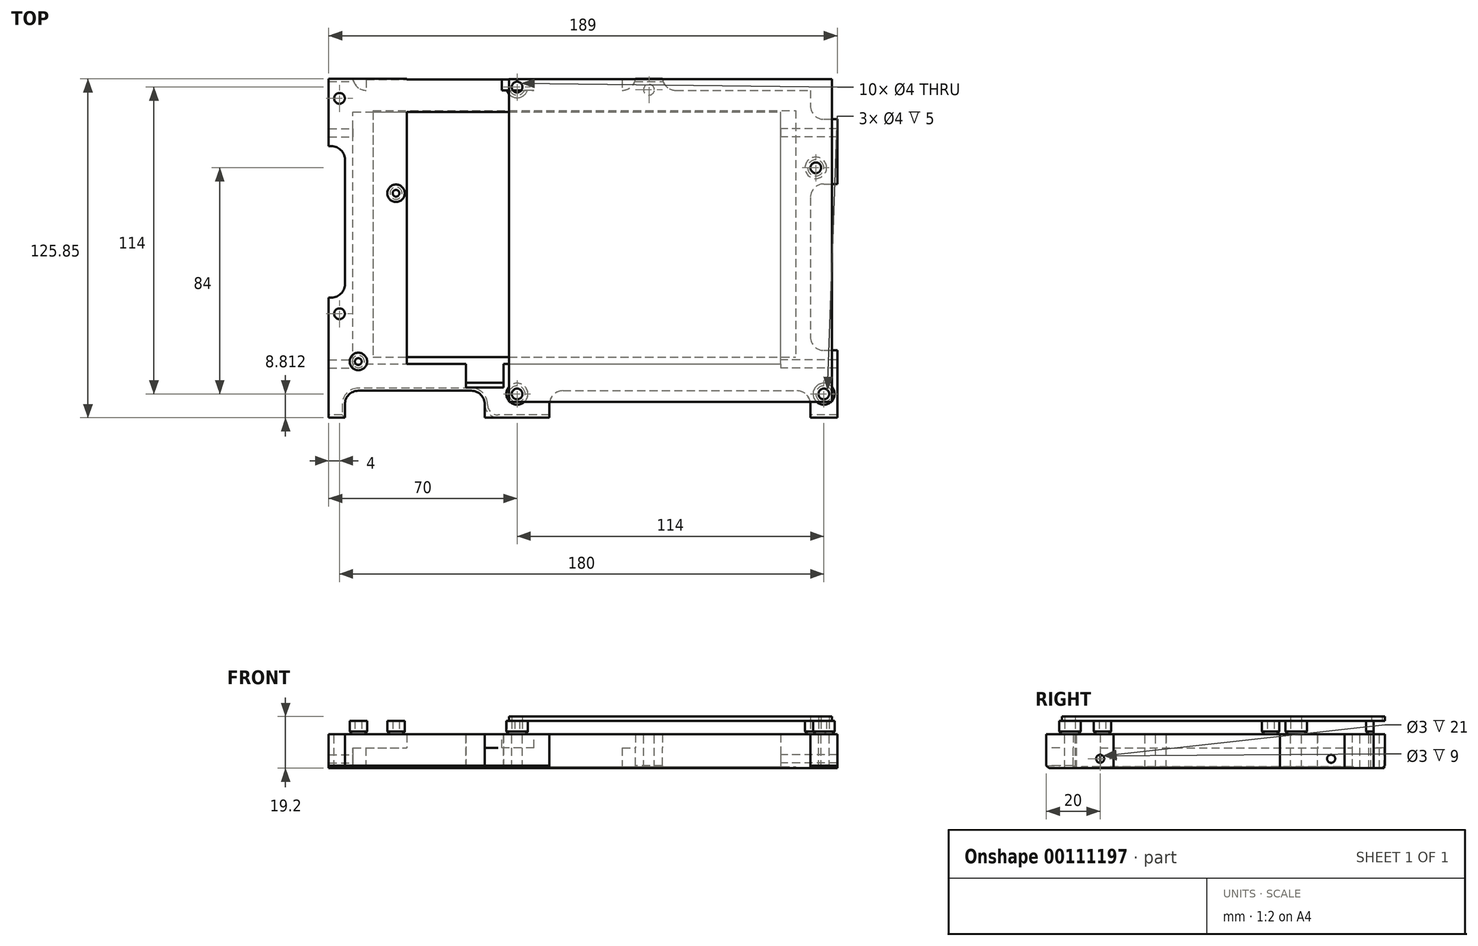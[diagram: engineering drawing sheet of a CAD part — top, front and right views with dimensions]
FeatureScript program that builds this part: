
annotation { "Feature Type Name" : "Feature", "Feature Type Description" : "" }
export const myFeature = defineFeature(function(context is Context, id is Id, definition is map)
    precondition{}
    {
        {
            var Q0;
            Q0=qCreatedBy(makeId("Top.planeOp"),FACE);
            var sketch = newSketch(context, id + "F0", { "sketchPlane" : qUnion([Q0])});
            skLineSegment(sketch, "E0.bottom", {"start": v(0, 0) * mm, "end": v(120, 0) * mm});
            skLineSegment(sketch, "E0.top", {"start": v(0, 120) * mm, "end": v(120, 120) * mm});
            skLineSegment(sketch, "E0.left", {"start": v(0, 0) * mm, "end": v(0, 120) * mm});
            skLineSegment(sketch, "E0.right", {"start": v(120, 0) * mm, "end": v(120, 120) * mm});
            skCircle(sketch, "E1", {"center": v(3, 117) * mm, "radius": 2 * mm});
            skCircle(sketch, "E2", {"center": v(3, 3) * mm, "radius": 2 * mm});
            skCircle(sketch, "E3", {"center": v(117, 3) * mm, "radius": 2 * mm});
            skCircle(sketch, "E4", {"center": v(114, 87) * mm, "radius": 2 * mm});
            skSolve(sketch);
        }
        {
            var Q0;
            Q0 = qSketchRegion(id + "F0", true);
            extrude(context, id + "F1", {"entities" : qUnion([Q0]), "depth" : 1.6 * mm});
        }
        {
            var Q0;
            Q0=makeQuery(id+"F1.opExtrude","SWEPT_BODY",BODY,{"disambiguationData":[OSD([sQuery(id+"F0.wireOp",EDGE,"E0.bottom"),sQuery(id+"F0.wireOp",EDGE,"E0.top"),sQuery(id+"F0.wireOp",EDGE,"E0.left"),sQuery(id+"F0.wireOp",EDGE,"E0.right"),sQuery(id+"F0.wireOp",EDGE,"E1"),sQuery(id+"F0.wireOp",EDGE,"E2"),sQuery(id+"F0.wireOp",EDGE,"E3"),sQuery(id+"F0.wireOp",EDGE,"E4")])]});
            var Q1;
            Q1=qCreatedBy(makeId("Origin.pointOp"),VERTEX);
            transform(context, id + "F2", {"entities" : qUnion([Q0]), "transformType" : TransformType.TRANSLATION_3D, "dx" : 58 * mm, "dy" : -7.2 * mm, "dz" : 17 * mm, "makeCopy" : false});
        }
        {
            var Q0;
            Q0=qCreatedBy(makeId("Top.planeOp"),FACE);
            var sketch = newSketch(context, id + "F3", { "sketchPlane" : qUnion([Q0])});
            skLineSegment(sketch, "E5.bottom", {"start": v(0, 0) * mm, "end": v(167, 0) * mm});
            skLineSegment(sketch, "E5.top", {"start": v(0, 105.6) * mm, "end": v(167, 105.6) * mm});
            skLineSegment(sketch, "E5.left", {"start": v(0, 0) * mm, "end": v(0, 105.6) * mm});
            skLineSegment(sketch, "E5.right", {"start": v(167, 0) * mm, "end": v(167, 105.6) * mm});
            skLineSegment(sketch, "E6.bottom", {"start": v(7.5, 101.1) * mm, "end": v(164.5, 101.1) * mm});
            skLineSegment(sketch, "E6.top", {"start": v(7.5, 9.5) * mm, "end": v(164.5, 9.5) * mm});
            skLineSegment(sketch, "E6.left", {"start": v(7.5, 101.1) * mm, "end": v(7.5, 9.5) * mm});
            skLineSegment(sketch, "E6.right", {"start": v(164.5, 101.1) * mm, "end": v(164.5, 9.5) * mm});
            skLineSegment(sketch, "E7.bottom", {"start": v(-3, 108.6) * mm, "end": v(170, 108.6) * mm});
            skLineSegment(sketch, "E7.top", {"start": v(-3, -3) * mm, "end": v(170, -3) * mm});
            skLineSegment(sketch, "E7.left", {"start": v(-3, 108.6) * mm, "end": v(-3, -3) * mm});
            skLineSegment(sketch, "E7.right", {"start": v(170, 108.6) * mm, "end": v(170, -3) * mm});
            skCircle(sketch, "E8", {"center": v(-5, 25.6) * mm, "radius": 2 * mm});
            skCircle(sketch, "E9", {"center": v(172, 79.81) * mm, "radius": 2 * mm});
            skCircle(sketch, "E10", {"center": v(175, -4.19) * mm, "radius": 2 * mm});
            skCircle(sketch, "E11", {"center": v(61, -4.19) * mm, "radius": 2 * mm});
            skCircle(sketch, "E12", {"center": v(110, 108.81) * mm, "radius": 2 * mm});
            skCircle(sketch, "E13", {"center": v(-5, 105.6) * mm, "radius": 2 * mm});
            skLineSegment(sketch, "E14.bottom", {"start": v(170, 97.85) * mm, "end": v(180, 97.85) * mm});
            skLineSegment(sketch, "E14.top", {"start": v(170, 73.81) * mm, "end": v(180, 73.81) * mm});
            skLineSegment(sketch, "E14.left", {"start": v(170, 97.85) * mm, "end": v(170, 73.81) * mm});
            skLineSegment(sketch, "E14.right", {"start": v(180, 97.85) * mm, "end": v(180, 73.81) * mm});
            skLineSegment(sketch, "E15.bottom", {"start": v(105, 108.6) * mm, "end": v(115, 108.6) * mm});
            skLineSegment(sketch, "E15.top", {"start": v(105, 112.85) * mm, "end": v(115, 112.85) * mm});
            skLineSegment(sketch, "E15.left", {"start": v(105, 108.6) * mm, "end": v(105, 112.85) * mm});
            skLineSegment(sketch, "E15.right", {"start": v(115, 108.6) * mm, "end": v(115, 112.85) * mm});
            skPoint(sketch, "E16", {"position": v(110, 112.85) * mm});
            skLineSegment(sketch, "E17.bottom", {"start": v(0, 87.85) * mm, "end": v(-9, 87.85) * mm});
            skLineSegment(sketch, "E17.top", {"start": v(0, 112.85) * mm, "end": v(-9, 112.85) * mm});
            skLineSegment(sketch, "E17.left", {"start": v(0, 87.85) * mm, "end": v(0, 112.85) * mm});
            skLineSegment(sketch, "E17.right", {"start": v(-9, 87.85) * mm, "end": v(-9, 112.85) * mm});
            skLineSegment(sketch, "E18.bottom", {"start": v(-3, 31.6) * mm, "end": v(-9, 31.6) * mm});
            skLineSegment(sketch, "E18.top", {"start": v(-3, -13) * mm, "end": v(-9, -13) * mm});
            skLineSegment(sketch, "E18.left", {"start": v(-3, 31.6) * mm, "end": v(-3, -13) * mm});
            skLineSegment(sketch, "E18.right", {"start": v(-9, 31.6) * mm, "end": v(-9, -13) * mm});
            skLineSegment(sketch, "E19.bottom", {"start": v(48.98, -3) * mm, "end": v(73.02, -3) * mm});
            skLineSegment(sketch, "E19.top", {"start": v(48.98, -13) * mm, "end": v(73.02, -13) * mm});
            skLineSegment(sketch, "E19.left", {"start": v(48.98, -3) * mm, "end": v(48.98, -13) * mm});
            skLineSegment(sketch, "E19.right", {"start": v(73.02, -3) * mm, "end": v(73.02, -13) * mm});
            skPoint(sketch, "E20", {"position": v(61, -13) * mm});
            skLineSegment(sketch, "E21.bottom", {"start": v(170, 12) * mm, "end": v(180, 12) * mm});
            skLineSegment(sketch, "E21.top", {"start": v(170, -13) * mm, "end": v(180, -13) * mm});
            skLineSegment(sketch, "E21.left", {"start": v(170, 12) * mm, "end": v(170, -13) * mm});
            skLineSegment(sketch, "E21.right", {"start": v(180, 12) * mm, "end": v(180, -13) * mm});
            skLineSegment(sketch, "E22.bottom", {"start": v(42, 0) * mm, "end": v(56, 0) * mm});
            skLineSegment(sketch, "E22.top", {"start": v(42, -1.78) * mm, "end": v(56, -1.78) * mm});
            skLineSegment(sketch, "E22.left", {"start": v(42, 0) * mm, "end": v(42, -1.78) * mm});
            skLineSegment(sketch, "E22.right", {"start": v(56, 0) * mm, "end": v(56, -1.78) * mm});
            skSolve(sketch);
        }
        {
            var Q0;
            Q0 = qSketchRegion(id + "F3", true);
            var Q1;
            {var subQ0=sQuery(id+"F3.wireOp",EDGE,"E7.left");var subQ1=sQuery(id+"F3.wireOp",EDGE,"E7.bottom");var subQ2=makeQuery(id+"F3.imprint","INTERSECT",VERTEX,{"derivedFrom":[subQ1,subQ0]});Q1=makeQuery(id+"F3.imprint","IMPRINT",FACE,{"disambiguationData":[TD([[makeQuery(id+"F3.imprint","IMPRINT",EDGE,{"disambiguationData":[TD([[subQ2,-1.0]])],"derivedFrom":subQ1}),-1.0]])]});}
            var Q2;
            {var subQ0=sQuery(id+"F3.wireOp",EDGE,"E5.left");var subQ1=sQuery(id+"F3.wireOp",EDGE,"E5.top");var subQ2=makeQuery(id+"F3.imprint","INTERSECT",VERTEX,{"derivedFrom":[subQ1,subQ0]});Q2=makeQuery(id+"F3.imprint","IMPRINT",FACE,{"disambiguationData":[TD([[makeQuery(id+"F3.imprint","IMPRINT",EDGE,{"disambiguationData":[TD([[subQ2,-1.0]])],"derivedFrom":subQ1}),-1.0]])]});}
            var Q3;
            Q3=makeQuery(id+"F3.imprint","IMPRINT",FACE,{"disambiguationData":[TD([[makeQuery(id+"F3.imprint","IMPRINT",EDGE,{"derivedFrom":sQuery(id+"F3.wireOp",EDGE,"E6.top")}),-1.0]])]});
            var Q4;
            {var subQ0=sQuery(id+"F3.wireOp",EDGE,"2effd1ed-b8a1-4a45-aa0b-9ccc5334acc0");var subQ1=sQuery(id+"F3.wireOp",EDGE,"E5.top");var subQ2=makeQuery(id+"F3.imprint","INTERSECT",VERTEX,{"disambiguationData":[OD(0.0)],"derivedFrom":[subQ1,subQ0]});Q4=makeQuery(id+"F3.imprint","IMPRINT",FACE,{"disambiguationData":[TD([[makeQuery(id+"F3.imprint","IMPRINT",EDGE,{"disambiguationData":[TD([[subQ2,-1.0]])],"derivedFrom":subQ1}),1.0]])]});}
            var Q5;
            {var subQ1=sQuery(id+"F3.wireOp",EDGE,"E5.top");var subQ4=sQuery(id+"F3.wireOp",EDGE,"5qO0xyPL-pihi-xQwt-uwnw-kNs82zO2X6Ps.left");var subQ9=makeQuery(id+"F3.imprint","INTERSECT",VERTEX,{"derivedFrom":[subQ1,subQ4]});Q5=makeQuery(id+"F3.imprint","IMPRINT",FACE,{"disambiguationData":[TD([[makeQuery(id+"F3.imprint","IMPRINT",EDGE,{"disambiguationData":[TD([[subQ9,-1.0]])],"derivedFrom":subQ1}),-1.0]])]});}
            var Q6;
            {var subQ0=sQuery(id+"F3.wireOp",EDGE,"2effd1ed-b8a1-4a45-aa0b-9ccc5334acc0");var subQ1=sQuery(id+"F3.wireOp",EDGE,"E5.top");var subQ2=makeQuery(id+"F3.imprint","INTERSECT",VERTEX,{"disambiguationData":[OD(0.0)],"derivedFrom":[subQ1,subQ0]});Q6=makeQuery(id+"F3.imprint","IMPRINT",FACE,{"disambiguationData":[TD([[makeQuery(id+"F3.imprint","IMPRINT",EDGE,{"disambiguationData":[TD([[subQ2,-1.0]])],"derivedFrom":subQ1}),-1.0]])]});}
            var Q7;
            {var subQ0=sQuery(id+"F3.wireOp",EDGE,"E7.right");var subQ1=sQuery(id+"F3.wireOp",EDGE,"E7.bottom");var subQ2=makeQuery(id+"F3.imprint","INTERSECT",VERTEX,{"derivedFrom":[subQ1,subQ0]});Q7=makeQuery(id+"F3.imprint","IMPRINT",FACE,{"disambiguationData":[TD([[makeQuery(id+"F3.imprint","IMPRINT",EDGE,{"disambiguationData":[TD([[subQ2,1.0]])],"derivedFrom":subQ1}),-1.0]])]});}
            var Q8;
            {var subQ0=sQuery(id+"F3.wireOp",EDGE,"E5.right");var subQ1=sQuery(id+"F3.wireOp",EDGE,"E5.top");var subQ2=makeQuery(id+"F3.imprint","INTERSECT",VERTEX,{"derivedFrom":[subQ1,subQ0]});Q8=makeQuery(id+"F3.imprint","IMPRINT",FACE,{"disambiguationData":[TD([[makeQuery(id+"F3.imprint","IMPRINT",EDGE,{"disambiguationData":[TD([[subQ2,1.0]])],"derivedFrom":subQ1}),-1.0]])]});}
            var Q9;
            {var subQ0=sQuery(id+"F3.wireOp",EDGE,"E7.right");var subQ1=sQuery(id+"F3.wireOp",EDGE,"E7.top");var subQ2=makeQuery(id+"F3.imprint","INTERSECT",VERTEX,{"derivedFrom":[subQ1,subQ0]});Q9=makeQuery(id+"F3.imprint","IMPRINT",FACE,{"disambiguationData":[TD([[makeQuery(id+"F3.imprint","IMPRINT",EDGE,{"disambiguationData":[TD([[subQ2,1.0]])],"derivedFrom":subQ1}),1.0]])]});}
            var Q10;
            {var subQ0=sQuery(id+"F3.wireOp",EDGE,"E5.right");var subQ1=sQuery(id+"F3.wireOp",EDGE,"E5.bottom");var subQ2=makeQuery(id+"F3.imprint","INTERSECT",VERTEX,{"derivedFrom":[subQ1,subQ0]});Q10=makeQuery(id+"F3.imprint","IMPRINT",FACE,{"disambiguationData":[TD([[makeQuery(id+"F3.imprint","IMPRINT",EDGE,{"disambiguationData":[TD([[subQ2,1.0]])],"derivedFrom":subQ1}),1.0]])]});}
            var Q11;
            {var subQ0=sQuery(id+"F3.wireOp",EDGE,"ad071df0-f90b-4ec1-959f-0245dd2d0ab3");var subQ1=sQuery(id+"F3.wireOp",EDGE,"E5.bottom");var subQ2=makeQuery(id+"F3.imprint","INTERSECT",VERTEX,{"disambiguationData":[OD(0.0)],"derivedFrom":[subQ1,subQ0]});Q11=makeQuery(id+"F3.imprint","IMPRINT",FACE,{"disambiguationData":[TD([[makeQuery(id+"F3.imprint","IMPRINT",EDGE,{"disambiguationData":[TD([[subQ2,-1.0]])],"derivedFrom":subQ1}),-1.0]])]});}
            var Q12;
            {var subQ0=sQuery(id+"F3.wireOp",EDGE,"ad071df0-f90b-4ec1-959f-0245dd2d0ab3");var subQ1=sQuery(id+"F3.wireOp",EDGE,"E5.bottom");var subQ2=makeQuery(id+"F3.imprint","INTERSECT",VERTEX,{"disambiguationData":[OD(0.0)],"derivedFrom":[subQ1,subQ0]});Q12=makeQuery(id+"F3.imprint","IMPRINT",FACE,{"disambiguationData":[TD([[makeQuery(id+"F3.imprint","IMPRINT",EDGE,{"disambiguationData":[TD([[subQ2,-1.0]])],"derivedFrom":subQ1}),1.0]])]});}
            var Q13;
            {var subQ6=sQuery(id+"F3.wireOp",EDGE,"Atmeq1sb-bySC-zfRP-H8Tq-u65LBA7bltvi.bottom");Q13=makeQuery(id+"F3.imprint","IMPRINT",FACE,{"disambiguationData":[TD([[makeQuery(id+"F3.imprint","IMPRINT",EDGE,{"derivedFrom":subQ6}),-1.0]])]});}
            var Q14;
            {var subQ0=sQuery(id+"F3.wireOp",EDGE,"E7.left");var subQ1=sQuery(id+"F3.wireOp",EDGE,"E7.top");var subQ2=makeQuery(id+"F3.imprint","INTERSECT",VERTEX,{"derivedFrom":[subQ1,subQ0]});Q14=makeQuery(id+"F3.imprint","IMPRINT",FACE,{"disambiguationData":[TD([[makeQuery(id+"F3.imprint","IMPRINT",EDGE,{"disambiguationData":[TD([[subQ2,-1.0]])],"derivedFrom":subQ1}),1.0]])]});}
            var Q15;
            {var subQ0=sQuery(id+"F3.wireOp",EDGE,"E5.left");var subQ1=sQuery(id+"F3.wireOp",EDGE,"E5.bottom");var subQ2=makeQuery(id+"F3.imprint","INTERSECT",VERTEX,{"derivedFrom":[subQ1,subQ0]});Q15=makeQuery(id+"F3.imprint","IMPRINT",FACE,{"disambiguationData":[TD([[makeQuery(id+"F3.imprint","IMPRINT",EDGE,{"disambiguationData":[TD([[subQ2,-1.0]])],"derivedFrom":subQ1}),1.0]])]});}
            var Q16;
            Q16=makeQuery(id+"F3.imprint","IMPRINT",FACE,{"disambiguationData":[TD([[makeQuery(id+"F3.imprint","IMPRINT",EDGE,{"derivedFrom":sQuery(id+"F3.wireOp",EDGE,"E22.bottom")}),-1.0]])]});
            extrude(context, id + "F4", {"entities" : qUnion([Q0, Q1, Q2, Q3, Q4, Q5, Q6, Q7, Q8, Q9, Q10, Q11, Q12, Q13, Q14, Q15, Q16]), "oppositeDirection" : true, "depth" : 0.6 * mm});
        }
        {
            var Q0;
            Q0 = qSketchRegion(id + "F3", true);
            var Q1;
            {var subQ0=sQuery(id+"F3.wireOp",EDGE,"E7.left");var subQ1=sQuery(id+"F3.wireOp",EDGE,"E7.bottom");var subQ2=makeQuery(id+"F3.imprint","INTERSECT",VERTEX,{"derivedFrom":[subQ1,subQ0]});Q1=makeQuery(id+"F3.imprint","IMPRINT",FACE,{"disambiguationData":[TD([[makeQuery(id+"F3.imprint","IMPRINT",EDGE,{"disambiguationData":[TD([[subQ2,-1.0]])],"derivedFrom":subQ1}),-1.0]])]});}
            var Q2;
            {var subQ0=sQuery(id+"F3.wireOp",EDGE,"2effd1ed-b8a1-4a45-aa0b-9ccc5334acc0");var subQ1=sQuery(id+"F3.wireOp",EDGE,"E5.top");var subQ2=makeQuery(id+"F3.imprint","INTERSECT",VERTEX,{"disambiguationData":[OD(0.0)],"derivedFrom":[subQ1,subQ0]});Q2=makeQuery(id+"F3.imprint","IMPRINT",FACE,{"disambiguationData":[TD([[makeQuery(id+"F3.imprint","IMPRINT",EDGE,{"disambiguationData":[TD([[subQ2,-1.0]])],"derivedFrom":subQ1}),1.0]])]});}
            var Q3;
            {var subQ0=sQuery(id+"F3.wireOp",EDGE,"E7.right");var subQ1=sQuery(id+"F3.wireOp",EDGE,"E7.bottom");var subQ2=makeQuery(id+"F3.imprint","INTERSECT",VERTEX,{"derivedFrom":[subQ1,subQ0]});Q3=makeQuery(id+"F3.imprint","IMPRINT",FACE,{"disambiguationData":[TD([[makeQuery(id+"F3.imprint","IMPRINT",EDGE,{"disambiguationData":[TD([[subQ2,1.0]])],"derivedFrom":subQ1}),-1.0]])]});}
            var Q4;
            {var subQ0=sQuery(id+"F3.wireOp",EDGE,"E7.right");var subQ1=sQuery(id+"F3.wireOp",EDGE,"E7.top");var subQ2=makeQuery(id+"F3.imprint","INTERSECT",VERTEX,{"derivedFrom":[subQ1,subQ0]});Q4=makeQuery(id+"F3.imprint","IMPRINT",FACE,{"disambiguationData":[TD([[makeQuery(id+"F3.imprint","IMPRINT",EDGE,{"disambiguationData":[TD([[subQ2,1.0]])],"derivedFrom":subQ1}),1.0]])]});}
            var Q5;
            {var subQ0=sQuery(id+"F3.wireOp",EDGE,"ad071df0-f90b-4ec1-959f-0245dd2d0ab3");var subQ1=sQuery(id+"F3.wireOp",EDGE,"E5.bottom");var subQ9=makeQuery(id+"F3.imprint","INTERSECT",VERTEX,{"disambiguationData":[OD(0.0)],"derivedFrom":[subQ1,subQ0]});Q5=makeQuery(id+"F3.imprint","IMPRINT",FACE,{"disambiguationData":[TD([[makeQuery(id+"F3.imprint","IMPRINT",EDGE,{"disambiguationData":[TD([[subQ9,-1.0]])],"derivedFrom":subQ1}),-1.0]])]});}
            var Q6;
            {var subQ0=sQuery(id+"F3.wireOp",EDGE,"E7.left");var subQ1=sQuery(id+"F3.wireOp",EDGE,"E7.top");var subQ2=makeQuery(id+"F3.imprint","INTERSECT",VERTEX,{"derivedFrom":[subQ1,subQ0]});Q6=makeQuery(id+"F3.imprint","IMPRINT",FACE,{"disambiguationData":[TD([[makeQuery(id+"F3.imprint","IMPRINT",EDGE,{"disambiguationData":[TD([[subQ2,-1.0]])],"derivedFrom":subQ1}),1.0]])]});}
            extrude(context, id + "F5", {"entities" : qUnion([Q0, Q1, Q2, Q3, Q4, Q5, Q6]), "depth" : 7 * mm});
        }
        {
            var Q0;
            Q0=makeQuery(id+"F4.opExtrude","SWEPT_BODY",BODY,{"disambiguationData":[OSD([sQuery(id+"F3.wireOp",EDGE,"E6.bottom"),sQuery(id+"F3.wireOp",EDGE,"E6.top"),sQuery(id+"F3.wireOp",EDGE,"E6.left"),sQuery(id+"F3.wireOp",EDGE,"E6.right"),sQuery(id+"F3.wireOp",EDGE,"E7.bottom"),sQuery(id+"F3.wireOp",EDGE,"E7.top"),sQuery(id+"F3.wireOp",EDGE,"E7.left"),sQuery(id+"F3.wireOp",EDGE,"E7.right"),sQuery(id+"F3.wireOp",EDGE,"v2m9uQtL-PCc6-w1WJ-7x69-SFVGcdV9juYy"),sQuery(id+"F3.wireOp",EDGE,"E8"),sQuery(id+"F3.wireOp",EDGE,"b3632d57-43a6-43b2-8df0-308d764fbdf1"),sQuery(id+"F3.wireOp",EDGE,"E9"),sQuery(id+"F3.wireOp",EDGE,"8d78386d-7bef-4069-aa0c-b06d9c6ee7e5"),sQuery(id+"F3.wireOp",EDGE,"E10"),sQuery(id+"F3.wireOp",EDGE,"ad071df0-f90b-4ec1-959f-0245dd2d0ab3"),sQuery(id+"F3.wireOp",EDGE,"E11"),sQuery(id+"F3.wireOp",EDGE,"2effd1ed-b8a1-4a45-aa0b-9ccc5334acc0"),sQuery(id+"F3.wireOp",EDGE,"E12"),sQuery(id+"F3.wireOp",EDGE,"f565c98e-65e2-452c-9097-589fedbe31dd"),sQuery(id+"F3.wireOp",EDGE,"E13"),sQuery(id+"F3.wireOp",EDGE,"9qAYj2DI-LqCA-QI6o-xDgW-T8vda7g123CK.top"),sQuery(id+"F3.wireOp",EDGE,"Q4LiiW50-2nHb-LRuc-Eouo-QSAKbSEKKer4.left"),sQuery(id+"F3.wireOp",EDGE,"Q4LiiW50-2nHb-LRuc-Eouo-QSAKbSEKKer4.right"),sQuery(id+"F3.wireOp",EDGE,"5qO0xyPL-pihi-xQwt-uwnw-kNs82zO2X6Ps.left"),sQuery(id+"F3.wireOp",EDGE,"5qO0xyPL-pihi-xQwt-uwnw-kNs82zO2X6Ps.right"),sQuery(id+"F3.wireOp",EDGE,"U4i4nSYP-nLCI-YEJG-py9I-UZ10o2biolml.bottom"),sQuery(id+"F3.wireOp",EDGE,"U4i4nSYP-nLCI-YEJG-py9I-UZ10o2biolml.top"),sQuery(id+"F3.wireOp",EDGE,"KcKhcV7Q-3VRU-i3kS-puIQ-PHzv1hmxkKIN.bottom"),sQuery(id+"F3.wireOp",EDGE,"KcKhcV7Q-3VRU-i3kS-puIQ-PHzv1hmxkKIN.top"),sQuery(id+"F3.wireOp",EDGE,"Atmeq1sb-bySC-zfRP-H8Tq-u65LBA7bltvi.left"),sQuery(id+"F3.wireOp",EDGE,"Atmeq1sb-bySC-zfRP-H8Tq-u65LBA7bltvi.right"),sQuery(id+"F3.wireOp",EDGE,"J8OOeMUS-M3e3-ra21-Acso-XBzhgOfx288U.bottom"),sQuery(id+"F3.wireOp",EDGE,"J8OOeMUS-M3e3-ra21-Acso-XBzhgOfx288U.top")])]});
            var Q1;
            Q1=makeQuery(id+"F5.opExtrude","SWEPT_BODY",BODY,{"disambiguationData":[OSD([sQuery(id+"F3.wireOp",EDGE,"E5.bottom"),sQuery(id+"F3.wireOp",EDGE,"E5.top"),sQuery(id+"F3.wireOp",EDGE,"E5.left"),sQuery(id+"F3.wireOp",EDGE,"E5.right"),sQuery(id+"F3.wireOp",EDGE,"E7.bottom"),sQuery(id+"F3.wireOp",EDGE,"E7.top"),sQuery(id+"F3.wireOp",EDGE,"E7.left"),sQuery(id+"F3.wireOp",EDGE,"E7.right"),sQuery(id+"F3.wireOp",EDGE,"v2m9uQtL-PCc6-w1WJ-7x69-SFVGcdV9juYy"),sQuery(id+"F3.wireOp",EDGE,"E8"),sQuery(id+"F3.wireOp",EDGE,"b3632d57-43a6-43b2-8df0-308d764fbdf1"),sQuery(id+"F3.wireOp",EDGE,"E9"),sQuery(id+"F3.wireOp",EDGE,"8d78386d-7bef-4069-aa0c-b06d9c6ee7e5"),sQuery(id+"F3.wireOp",EDGE,"E10"),sQuery(id+"F3.wireOp",EDGE,"ad071df0-f90b-4ec1-959f-0245dd2d0ab3"),sQuery(id+"F3.wireOp",EDGE,"E11"),sQuery(id+"F3.wireOp",EDGE,"2effd1ed-b8a1-4a45-aa0b-9ccc5334acc0"),sQuery(id+"F3.wireOp",EDGE,"E12"),sQuery(id+"F3.wireOp",EDGE,"f565c98e-65e2-452c-9097-589fedbe31dd"),sQuery(id+"F3.wireOp",EDGE,"E13"),sQuery(id+"F3.wireOp",EDGE,"9qAYj2DI-LqCA-QI6o-xDgW-T8vda7g123CK.bottom"),sQuery(id+"F3.wireOp",EDGE,"9qAYj2DI-LqCA-QI6o-xDgW-T8vda7g123CK.top"),sQuery(id+"F3.wireOp",EDGE,"Q4LiiW50-2nHb-LRuc-Eouo-QSAKbSEKKer4.left"),sQuery(id+"F3.wireOp",EDGE,"Q4LiiW50-2nHb-LRuc-Eouo-QSAKbSEKKer4.right"),sQuery(id+"F3.wireOp",EDGE,"5qO0xyPL-pihi-xQwt-uwnw-kNs82zO2X6Ps.left"),sQuery(id+"F3.wireOp",EDGE,"5qO0xyPL-pihi-xQwt-uwnw-kNs82zO2X6Ps.right"),sQuery(id+"F3.wireOp",EDGE,"U4i4nSYP-nLCI-YEJG-py9I-UZ10o2biolml.bottom"),sQuery(id+"F3.wireOp",EDGE,"U4i4nSYP-nLCI-YEJG-py9I-UZ10o2biolml.top"),sQuery(id+"F3.wireOp",EDGE,"KcKhcV7Q-3VRU-i3kS-puIQ-PHzv1hmxkKIN.bottom"),sQuery(id+"F3.wireOp",EDGE,"KcKhcV7Q-3VRU-i3kS-puIQ-PHzv1hmxkKIN.top"),sQuery(id+"F3.wireOp",EDGE,"Atmeq1sb-bySC-zfRP-H8Tq-u65LBA7bltvi.left"),sQuery(id+"F3.wireOp",EDGE,"Atmeq1sb-bySC-zfRP-H8Tq-u65LBA7bltvi.right"),sQuery(id+"F3.wireOp",EDGE,"J8OOeMUS-M3e3-ra21-Acso-XBzhgOfx288U.bottom"),sQuery(id+"F3.wireOp",EDGE,"J8OOeMUS-M3e3-ra21-Acso-XBzhgOfx288U.top")])]});
            booleanBodies(context, id + "F6", {"operationType" : BooleanOperationType.UNION, "tools" : qUnion([Q0, Q1])});
        }
        {
            var Q0;
            {var subQ0=sQuery(id+"F3.wireOp",EDGE,"E19.right");var subQ1=sQuery(id+"F3.wireOp",EDGE,"E19.bottom");var subQ2=sQuery(id+"F3.wireOp",EDGE,"E7.top");Q0=makeQuery(id+"F6.opBoolean","MERGE",EDGE,{"derivedFrom":[makeQuery(id+"F4.opExtrude","SWEPT_EDGE",EDGE,{"disambiguationData":[OSD([subQ2,subQ1,subQ0])]}),makeQuery(id+"F5.opExtrude","SWEPT_EDGE",EDGE,{"disambiguationData":[OSD([subQ2,subQ1,subQ0])]})]});}
            var Q1;
            {var subQ0=sQuery(id+"F3.wireOp",EDGE,"E19.left");var subQ1=sQuery(id+"F3.wireOp",EDGE,"E19.bottom");var subQ2=sQuery(id+"F3.wireOp",EDGE,"9qAYj2DI-LqCA-QI6o-xDgW-T8vda7g123CK.top");Q1=makeQuery(id+"F6.opBoolean","MERGE",EDGE,{"derivedFrom":[makeQuery(id+"F4.opExtrude","SWEPT_EDGE",EDGE,{"disambiguationData":[OSD([subQ2,subQ1,subQ0])]}),makeQuery(id+"F5.opExtrude","SWEPT_EDGE",EDGE,{"disambiguationData":[OSD([subQ2,subQ1,subQ0])]})]});}
            var Q2;
            {var subQ0=sQuery(id+"F3.wireOp",EDGE,"E21.left");var subQ1=sQuery(id+"F3.wireOp",EDGE,"E7.top");Q2=makeQuery(id+"F6.opBoolean","MERGE",EDGE,{"derivedFrom":[makeQuery(id+"F4.opExtrude","SWEPT_EDGE",EDGE,{"disambiguationData":[OSD([subQ1,subQ0])]}),makeQuery(id+"F5.opExtrude","SWEPT_EDGE",EDGE,{"disambiguationData":[OSD([subQ1,subQ0])]})]});}
            var Q3;
            {var subQ0=sQuery(id+"F3.wireOp",EDGE,"E21.left");var subQ1=sQuery(id+"F3.wireOp",EDGE,"E21.bottom");var subQ2=sQuery(id+"F3.wireOp",EDGE,"E7.right");Q3=makeQuery(id+"F6.opBoolean","MERGE",EDGE,{"derivedFrom":[makeQuery(id+"F4.opExtrude","SWEPT_EDGE",EDGE,{"disambiguationData":[OSD([subQ2,subQ1,subQ0])]}),makeQuery(id+"F5.opExtrude","SWEPT_EDGE",EDGE,{"disambiguationData":[OSD([subQ2,subQ1,subQ0])]})]});}
            var Q4;
            {var subQ0=sQuery(id+"F3.wireOp",EDGE,"E14.left");var subQ1=sQuery(id+"F3.wireOp",EDGE,"E14.top");var subQ2=sQuery(id+"F3.wireOp",EDGE,"E7.right");Q4=makeQuery(id+"F6.opBoolean","MERGE",EDGE,{"derivedFrom":[makeQuery(id+"F4.opExtrude","SWEPT_EDGE",EDGE,{"disambiguationData":[OSD([subQ2,subQ1,subQ0])]}),makeQuery(id+"F5.opExtrude","SWEPT_EDGE",EDGE,{"disambiguationData":[OSD([subQ2,subQ1,subQ0])]})]});}
            var Q5;
            {var subQ0=sQuery(id+"F3.wireOp",EDGE,"E14.left");var subQ1=sQuery(id+"F3.wireOp",EDGE,"E14.bottom");var subQ2=sQuery(id+"F3.wireOp",EDGE,"E7.right");Q5=makeQuery(id+"F6.opBoolean","MERGE",EDGE,{"derivedFrom":[makeQuery(id+"F4.opExtrude","SWEPT_EDGE",EDGE,{"disambiguationData":[OSD([subQ2,subQ1,subQ0])]}),makeQuery(id+"F5.opExtrude","SWEPT_EDGE",EDGE,{"disambiguationData":[OSD([subQ2,subQ1,subQ0])]})]});}
            var Q6;
            {var subQ0=sQuery(id+"F3.wireOp",EDGE,"E15.right");var subQ1=sQuery(id+"F3.wireOp",EDGE,"E15.bottom");var subQ2=sQuery(id+"F3.wireOp",EDGE,"E7.bottom");Q6=makeQuery(id+"F6.opBoolean","MERGE",EDGE,{"derivedFrom":[makeQuery(id+"F4.opExtrude","SWEPT_EDGE",EDGE,{"disambiguationData":[OSD([subQ2,subQ1,subQ0])]}),makeQuery(id+"F5.opExtrude","SWEPT_EDGE",EDGE,{"disambiguationData":[OSD([subQ2,subQ1,subQ0])]})]});}
            var Q7;
            {var subQ0=sQuery(id+"F3.wireOp",EDGE,"E15.left");var subQ1=sQuery(id+"F3.wireOp",EDGE,"E15.bottom");var subQ2=sQuery(id+"F3.wireOp",EDGE,"E7.bottom");Q7=makeQuery(id+"F6.opBoolean","MERGE",EDGE,{"derivedFrom":[makeQuery(id+"F4.opExtrude","SWEPT_EDGE",EDGE,{"disambiguationData":[OSD([subQ2,subQ1,subQ0])]}),makeQuery(id+"F5.opExtrude","SWEPT_EDGE",EDGE,{"disambiguationData":[OSD([subQ2,subQ1,subQ0])]})]});}
            var Q8;
            {var subQ0=sQuery(id+"F3.wireOp",EDGE,"E17.left");var subQ1=sQuery(id+"F3.wireOp",EDGE,"E7.bottom");Q8=makeQuery(id+"F6.opBoolean","MERGE",EDGE,{"derivedFrom":[makeQuery(id+"F4.opExtrude","SWEPT_EDGE",EDGE,{"disambiguationData":[OSD([subQ1,subQ0])]}),makeQuery(id+"F5.opExtrude","SWEPT_EDGE",EDGE,{"disambiguationData":[OSD([subQ1,subQ0])]})]});}
            var Q9;
            {var subQ0=sQuery(id+"F3.wireOp",EDGE,"E17.bottom");var subQ1=sQuery(id+"F3.wireOp",EDGE,"E7.left");Q9=makeQuery(id+"F6.opBoolean","MERGE",EDGE,{"derivedFrom":[makeQuery(id+"F4.opExtrude","SWEPT_EDGE",EDGE,{"disambiguationData":[OSD([subQ1,subQ0])]}),makeQuery(id+"F5.opExtrude","SWEPT_EDGE",EDGE,{"disambiguationData":[OSD([subQ1,subQ0])]})]});}
            var Q10;
            {var subQ0=sQuery(id+"F3.wireOp",EDGE,"E18.left");var subQ1=sQuery(id+"F3.wireOp",EDGE,"E18.bottom");var subQ2=sQuery(id+"F3.wireOp",EDGE,"E7.left");Q10=makeQuery(id+"F6.opBoolean","MERGE",EDGE,{"derivedFrom":[makeQuery(id+"F4.opExtrude","SWEPT_EDGE",EDGE,{"disambiguationData":[OSD([subQ2,subQ1,subQ0])]}),makeQuery(id+"F5.opExtrude","SWEPT_EDGE",EDGE,{"disambiguationData":[OSD([subQ2,subQ1,subQ0])]})]});}
            var Q11;
            {var subQ0=sQuery(id+"F3.wireOp",EDGE,"E18.left");var subQ1=sQuery(id+"F3.wireOp",EDGE,"E7.top");Q11=makeQuery(id+"F6.opBoolean","MERGE",EDGE,{"derivedFrom":[makeQuery(id+"F4.opExtrude","SWEPT_EDGE",EDGE,{"disambiguationData":[OSD([subQ1,subQ0])]}),makeQuery(id+"F5.opExtrude","SWEPT_EDGE",EDGE,{"disambiguationData":[OSD([subQ1,subQ0])]})]});}
            fillet(context, id + "F7", {"entities" : qUnion([Q0, Q1, Q2, Q3, Q4, Q5, Q6, Q7, Q8, Q9, Q10, Q11]), "radius" : 5 * mm, "tangentPropagation" : true, "allowEdgeOverflow" : false});
        }
        {
            var Q0;
            Q0=qCreatedBy(makeId("Right.planeOp"),FACE);
            var sketch = newSketch(context, id + "F8", { "sketchPlane" : qUnion([Q0])});
            skCircle(sketch, "E23", {"center": v(7, 2.9) * mm, "radius": 1.5 * mm});
            skCircle(sketch, "E24", {"center": v(92.85, 2.9) * mm, "radius": 1.5 * mm});
            skSolve(sketch);
        }
        {
            var Q0;
            Q0 = qSketchRegion(id + "F8", true);
            extrude(context, id + "F9", {"entities" : qUnion([Q0]), "operationType" : NewBodyOperationType.REMOVE, "endBound" : BoundingType.THROUGH_ALL, "depth" : 25 * mm});
        }
        {
            var Q0;
            Q0 = qSketchRegion(id + "F8", true);
            extrude(context, id + "F10", {"entities" : qUnion([Q0]), "operationType" : NewBodyOperationType.REMOVE, "endBound" : BoundingType.THROUGH_ALL, "oppositeDirection" : true, "depth" : 25 * mm});
        }
        {
            var Q0;
            Q0=makeQuery(id+"F4.opExtrude","CAP_EDGE",EDGE,{"disambiguationData":[OSD([sQuery(id+"F3.wireOp",EDGE,"E15.top")])],"isStart":false});
            var Q1;
            Q1=makeQuery(id+"F4.opExtrude","CAP_EDGE",EDGE,{"disambiguationData":[OSD([sQuery(id+"F3.wireOp",EDGE,"E17.top")])],"isStart":false});
            var Q2;
            Q2=makeQuery(id+"F4.opExtrude","CAP_EDGE",EDGE,{"disambiguationData":[OSD([sQuery(id+"F3.wireOp",EDGE,"E18.top")])],"isStart":false});
            var Q3;
            Q3=makeQuery(id+"F4.opExtrude","CAP_EDGE",EDGE,{"disambiguationData":[OSD([sQuery(id+"F3.wireOp",EDGE,"E19.top")])],"isStart":false});
            var Q4;
            Q4=makeQuery(id+"F4.opExtrude","CAP_EDGE",EDGE,{"disambiguationData":[OSD([sQuery(id+"F3.wireOp",EDGE,"E21.top")])],"isStart":false});
            chamfer(context, id + "F11", {"entities" : qUnion([Q0, Q1, Q2, Q3, Q4]), "width" : 1 * mm, "tangentPropagation" : true});
        }
        {
            var Q0;
            Q0 = qSketchRegion(id + "F3", true);
            var Q1;
            Q1=makeQuery(id+"F3.imprint","IMPRINT",FACE,{"disambiguationData":[TD([[makeQuery(id+"F3.imprint","IMPRINT",EDGE,{"derivedFrom":sQuery(id+"F3.wireOp",EDGE,"E22.bottom")}),-1.0]])]});
            extrude(context, id + "F12", {"entities" : qUnion([Q0, Q1]), "depth" : 5 * mm});
        }
        {
            var Q0;
            Q0=makeQuery(id+"F12.opExtrude","SWEPT_BODY",BODY,{"disambiguationData":[OSD([sQuery(id+"F3.wireOp",EDGE,"E5.bottom"),sQuery(id+"F3.wireOp",EDGE,"E5.top"),sQuery(id+"F3.wireOp",EDGE,"E5.left"),sQuery(id+"F3.wireOp",EDGE,"E5.right"),sQuery(id+"F3.wireOp",EDGE,"E7.bottom"),sQuery(id+"F3.wireOp",EDGE,"E7.top"),sQuery(id+"F3.wireOp",EDGE,"E7.left"),sQuery(id+"F3.wireOp",EDGE,"E7.right"),sQuery(id+"F3.wireOp",EDGE,"E8"),sQuery(id+"F3.wireOp",EDGE,"E9"),sQuery(id+"F3.wireOp",EDGE,"E10"),sQuery(id+"F3.wireOp",EDGE,"E11"),sQuery(id+"F3.wireOp",EDGE,"E12"),sQuery(id+"F3.wireOp",EDGE,"E13"),sQuery(id+"F3.wireOp",EDGE,"E14.bottom"),sQuery(id+"F3.wireOp",EDGE,"E14.top"),sQuery(id+"F3.wireOp",EDGE,"E14.right"),sQuery(id+"F3.wireOp",EDGE,"E15.top"),sQuery(id+"F3.wireOp",EDGE,"E15.left"),sQuery(id+"F3.wireOp",EDGE,"E15.right"),sQuery(id+"F3.wireOp",EDGE,"E17.bottom"),sQuery(id+"F3.wireOp",EDGE,"E17.top"),sQuery(id+"F3.wireOp",EDGE,"E17.left"),sQuery(id+"F3.wireOp",EDGE,"E17.right"),sQuery(id+"F3.wireOp",EDGE,"E18.bottom"),sQuery(id+"F3.wireOp",EDGE,"E18.top"),sQuery(id+"F3.wireOp",EDGE,"E18.left"),sQuery(id+"F3.wireOp",EDGE,"E18.right"),sQuery(id+"F3.wireOp",EDGE,"E19.top"),sQuery(id+"F3.wireOp",EDGE,"E19.left"),sQuery(id+"F3.wireOp",EDGE,"E19.right"),sQuery(id+"F3.wireOp",EDGE,"E21.bottom"),sQuery(id+"F3.wireOp",EDGE,"E21.top"),sQuery(id+"F3.wireOp",EDGE,"E21.left"),sQuery(id+"F3.wireOp",EDGE,"E21.right"),sQuery(id+"F3.wireOp",EDGE,"E22.top"),sQuery(id+"F3.wireOp",EDGE,"E22.left"),sQuery(id+"F3.wireOp",EDGE,"E22.right")])]});
            transform(context, id + "F13", {"entities" : qUnion([Q0]), "transformType" : TransformType.TRANSLATION_3D, "dx" : 0 * mm, "dy" : 0 * mm, "dz" : 7 * mm, "makeCopy" : false});
        }
        {
            var Q0;
            Q0=makeQuery(id+"F12.opExtrude","SWEPT_FACE",FACE,{"disambiguationData":[OSD([sQuery(id+"F3.wireOp",EDGE,"E5.left"),sQuery(id+"F3.wireOp",EDGE,"E17.left")])]});
            extrude(context, id + "F14", {"entities" : qUnion([Q0]), "operationType" : NewBodyOperationType.ADD, "depth" : 20 * mm});
        }
        {
            var Q0;
            Q0=makeQuery(id+"F12.opExtrude","SWEPT_FACE",FACE,{"disambiguationData":[OSD([sQuery(id+"F3.wireOp",EDGE,"E5.right")])]});
            extrude(context, id + "F15", {"entities" : qUnion([Q0]), "operationType" : NewBodyOperationType.ADD, "depth" : 8 * mm});
        }
        {
            var Q0;
            Q0=makeQuery(id+"F12.opExtrude","SWEPT_FACE",FACE,{"disambiguationData":[OSD([sQuery(id+"F3.wireOp",EDGE,"E5.bottom"),sQuery(id+"F3.wireOp",EDGE,"E22.bottom")])]});
            extrude(context, id + "F16", {"entities" : qUnion([Q0]), "operationType" : NewBodyOperationType.ADD, "depth" : 7 * mm});
        }
        {
            var Q0;
            Q0=makeQuery(id+"F12.opExtrude","SWEPT_FACE",FACE,{"disambiguationData":[OSD([sQuery(id+"F3.wireOp",EDGE,"E5.top")])]});
            extrude(context, id + "F17", {"entities" : qUnion([Q0]), "operationType" : NewBodyOperationType.ADD, "depth" : 5 * mm});
        }
        {
            var Q0;
            {var subQ0=sQuery(id+"F3.wireOp",EDGE,"E7.bottom");Q0=makeQuery(id+"F12.opExtrude","SWEPT_FACE",FACE,{"disambiguationData":[OSD([subQ0]),TDD([makeQuery(id+"F3.imprint","IMPRINT",EDGE,{"disambiguationData":[TD([[makeQuery(id+"F3.imprint","INTERSECT",VERTEX,{"derivedFrom":[subQ0,sQuery(id+"F3.wireOp",EDGE,"E17.left")]}),-1.0]])],"derivedFrom":subQ0})])]});}
            var sketch = newSketch(context, id + "F18", { "sketchPlane" : qUnion([Q0])});
            skLineSegment(sketch, "E25.bottom", {"start": v(-67.3, 7) * mm, "end": v(-55.3, 7) * mm});
            skLineSegment(sketch, "E25.top", {"start": v(-67.3, 12) * mm, "end": v(-55.3, 12) * mm});
            skLineSegment(sketch, "E25.left", {"start": v(-67.3, 7) * mm, "end": v(-67.3, 12) * mm});
            skLineSegment(sketch, "E25.right", {"start": v(-55.3, 7) * mm, "end": v(-55.3, 12) * mm});
            skPoint(sketch, "E26", {"position": v(-61.3, 7) * mm});
            skSolve(sketch);
        }
        {
            var Q0;
            Q0=makeQuery(id+"F18.imprint","IMPRINT",FACE,{"disambiguationData":[TD([[makeQuery(id+"F18.imprint","IMPRINT",EDGE,{"derivedFrom":sQuery(id+"F18.wireOp",EDGE,"E25.bottom")}),-1.0]])]});
            extrude(context, id + "F19", {"entities" : qUnion([Q0]), "operationType" : NewBodyOperationType.ADD, "depth" : 4 * mm});
        }
        {
            var Q0;
            {var subQ0=sQuery(id+"F3.wireOp",EDGE,"E5.top");var subQ1=sQuery(id+"F3.wireOp",EDGE,"E22.bottom");var subQ2=sQuery(id+"F3.wireOp",EDGE,"E5.bottom");var subQ3=sQuery(id+"F3.wireOp",EDGE,"E5.right");var subQ4=sQuery(id+"F3.wireOp",EDGE,"E17.left");var subQ5=sQuery(id+"F3.wireOp",EDGE,"E5.left");Q0=makeQuery(id+"F19.boolean.opBoolean","MERGE",FACE,{"derivedFrom":[makeQuery(id+"F17.boolean.opBoolean","MERGE",FACE,{"derivedFrom":[makeQuery(id+"F16.boolean.opBoolean","MERGE",FACE,{"derivedFrom":[makeQuery(id+"F15.boolean.opBoolean","MERGE",FACE,{"derivedFrom":[makeQuery(id+"F14.boolean.opBoolean","MERGE",FACE,{"derivedFrom":[makeQuery(id+"F12.opExtrude","CAP_FACE",FACE,{"disambiguationData":[OSD([subQ2,subQ0,subQ5,subQ3,sQuery(id+"F3.wireOp",EDGE,"E7.bottom"),sQuery(id+"F3.wireOp",EDGE,"E7.top"),sQuery(id+"F3.wireOp",EDGE,"E7.left"),sQuery(id+"F3.wireOp",EDGE,"E7.right"),sQuery(id+"F3.wireOp",EDGE,"E8"),sQuery(id+"F3.wireOp",EDGE,"E9"),sQuery(id+"F3.wireOp",EDGE,"E10"),sQuery(id+"F3.wireOp",EDGE,"E11"),sQuery(id+"F3.wireOp",EDGE,"E12"),sQuery(id+"F3.wireOp",EDGE,"E13"),sQuery(id+"F3.wireOp",EDGE,"E14.bottom"),sQuery(id+"F3.wireOp",EDGE,"E14.top"),sQuery(id+"F3.wireOp",EDGE,"E14.right"),sQuery(id+"F3.wireOp",EDGE,"E15.top"),sQuery(id+"F3.wireOp",EDGE,"E15.left"),sQuery(id+"F3.wireOp",EDGE,"E15.right"),sQuery(id+"F3.wireOp",EDGE,"E17.bottom"),sQuery(id+"F3.wireOp",EDGE,"E17.top"),subQ4,sQuery(id+"F3.wireOp",EDGE,"E17.right"),sQuery(id+"F3.wireOp",EDGE,"E18.bottom"),sQuery(id+"F3.wireOp",EDGE,"E18.top"),sQuery(id+"F3.wireOp",EDGE,"E18.left"),sQuery(id+"F3.wireOp",EDGE,"E18.right"),sQuery(id+"F3.wireOp",EDGE,"E19.top"),sQuery(id+"F3.wireOp",EDGE,"E19.left"),sQuery(id+"F3.wireOp",EDGE,"E19.right"),sQuery(id+"F3.wireOp",EDGE,"E21.bottom"),sQuery(id+"F3.wireOp",EDGE,"E21.top"),sQuery(id+"F3.wireOp",EDGE,"E21.left"),sQuery(id+"F3.wireOp",EDGE,"E21.right"),subQ1])],"isStart":false}),makeQuery(id+"F14.opExtrude","SWEPT_FACE",FACE,{"disambiguationData":[OSD([subQ5,subQ4]),TDD([makeQuery(id+"F12.opExtrude","CAP_EDGE",EDGE,{"disambiguationData":[OSD([subQ5,subQ4])],"isStart":false})])]})]}),makeQuery(id+"F15.opExtrude","SWEPT_FACE",FACE,{"disambiguationData":[OSD([subQ3]),TDD([makeQuery(id+"F12.opExtrude","CAP_EDGE",EDGE,{"disambiguationData":[OSD([subQ3])],"isStart":false})])]})]}),makeQuery(id+"F16.opExtrude","SWEPT_FACE",FACE,{"disambiguationData":[OSD([subQ2,subQ1]),TDD([makeQuery(id+"F12.opExtrude","CAP_EDGE",EDGE,{"disambiguationData":[OSD([subQ2,subQ1])],"isStart":false})])]})]}),makeQuery(id+"F17.opExtrude","SWEPT_FACE",FACE,{"disambiguationData":[OSD([subQ0]),TDD([makeQuery(id+"F12.opExtrude","CAP_EDGE",EDGE,{"disambiguationData":[OSD([subQ0])],"isStart":false})])]})]}),makeQuery(id+"F19.opExtrude","SWEPT_FACE",FACE,{"disambiguationData":[OSD([sQuery(id+"F18.wireOp",EDGE,"E25.top")])]})]});}
            var sketch = newSketch(context, id + "F20", { "sketchPlane" : qUnion([Q0])});
            skCircle(sketch, "E27", {"center": v(61, 109.81) * mm, "radius": 4 * mm});
            skCircle(sketch, "E28", {"center": v(172, 79.81) * mm, "radius": 4 * mm});
            skCircle(sketch, "E29", {"center": v(175, -4.19) * mm, "radius": 4 * mm});
            skCircle(sketch, "E30", {"center": v(61, -4.19) * mm, "radius": 4 * mm});
            skCircle(sketch, "E31", {"center": v(16, 70.36) * mm, "radius": 3.25 * mm});
            skCircle(sketch, "E32", {"center": v(2, 7.86) * mm, "radius": 3.25 * mm});
            skCircle(sketch, "E33", {"center": v(16, 70.36) * mm, "radius": 1.25 * mm});
            skCircle(sketch, "E34", {"center": v(2, 7.86) * mm, "radius": 1.25 * mm});
            skCircle(sketch, "E35", {"center": v(61, 109.81) * mm, "radius": 1.5 * mm});
            skSolve(sketch);
        }
        {
            var Q0;
            {var subQ0=sQuery(id+"F20.wireOp",EDGE,"E27");var subQ1=makeQuery(id+"F19.opExtrude","CAP_EDGE",EDGE,{"disambiguationData":[OSD([sQuery(id+"F18.wireOp",EDGE,"E25.top")])],"isStart":false});var subQ2=makeQuery(id+"F20.imprint","INTERSECT",VERTEX,{"disambiguationData":[OD(0.0)],"derivedFrom":[subQ1,subQ0]});Q0=makeQuery(id+"F20.imprint","IMPRINT",FACE,{"disambiguationData":[TD([[makeQuery(id+"F20.imprint","IMPRINT",EDGE,{"disambiguationData":[TD([[subQ2,-1.0]])],"derivedFrom":subQ0}),1.0]])]});}
            var Q1;
            Q1=makeQuery(id+"F20.imprint","IMPRINT",FACE,{"disambiguationData":[TD([[makeQuery(id+"F20.imprint","IMPRINT",EDGE,{"derivedFrom":sQuery(id+"F20.wireOp",EDGE,"E28")}),1.0]])]});
            var Q2;
            Q2=makeQuery(id+"F20.imprint","IMPRINT",FACE,{"disambiguationData":[TD([[makeQuery(id+"F20.imprint","IMPRINT",EDGE,{"derivedFrom":sQuery(id+"F20.wireOp",EDGE,"E30")}),1.0]])]});
            var Q3;
            Q3=makeQuery(id+"F20.imprint","IMPRINT",FACE,{"disambiguationData":[TD([[makeQuery(id+"F20.imprint","IMPRINT",EDGE,{"derivedFrom":sQuery(id+"F20.wireOp",EDGE,"E29")}),1.0]])]});
            var Q4;
            Q4=makeQuery(id+"F20.imprint","IMPRINT",FACE,{"disambiguationData":[TD([[makeQuery(id+"F20.imprint","IMPRINT",EDGE,{"derivedFrom":sQuery(id+"F20.wireOp",EDGE,"E31")}),1.0]])]});
            var Q5;
            Q5=makeQuery(id+"F20.imprint","IMPRINT",FACE,{"disambiguationData":[TD([[makeQuery(id+"F20.imprint","IMPRINT",EDGE,{"derivedFrom":sQuery(id+"F20.wireOp",EDGE,"E32")}),1.0]])]});
            extrude(context, id + "F21", {"entities" : qUnion([Q0, Q1, Q2, Q3, Q4, Q5]), "depth" : 5 * mm});
        }
        {
            var Q0;
            Q0=makeQuery(id+"F12.opExtrude","SWEPT_EDGE",EDGE,{"disambiguationData":[OSD([sQuery(id+"F3.wireOp",EDGE,"E7.top"),sQuery(id+"F3.wireOp",EDGE,"E18.left")])]});
            var Q1;
            Q1=makeQuery(id+"F12.opExtrude","SWEPT_EDGE",EDGE,{"disambiguationData":[OSD([sQuery(id+"F3.wireOp",EDGE,"E7.top"),sQuery(id+"F3.wireOp",EDGE,"E19.bottom"),sQuery(id+"F3.wireOp",EDGE,"E19.left")])]});
            var Q2;
            Q2=makeQuery(id+"F12.opExtrude","SWEPT_EDGE",EDGE,{"disambiguationData":[OSD([sQuery(id+"F3.wireOp",EDGE,"E7.left"),sQuery(id+"F3.wireOp",EDGE,"E18.bottom"),sQuery(id+"F3.wireOp",EDGE,"E18.left")])]});
            var Q3;
            Q3=makeQuery(id+"F12.opExtrude","SWEPT_EDGE",EDGE,{"disambiguationData":[OSD([sQuery(id+"F3.wireOp",EDGE,"E7.left"),sQuery(id+"F3.wireOp",EDGE,"E17.bottom")])]});
            var Q4;
            Q4=makeQuery(id+"F12.opExtrude","SWEPT_EDGE",EDGE,{"disambiguationData":[OSD([sQuery(id+"F3.wireOp",EDGE,"E7.bottom"),sQuery(id+"F3.wireOp",EDGE,"E17.left")])]});
            var Q5;
            Q5=makeQuery(id+"F19.opExtrude","CAP_EDGE",EDGE,{"disambiguationData":[OSD([sQuery(id+"F18.wireOp",EDGE,"E25.right")])],"isStart":true});
            var Q6;
            Q6=makeQuery(id+"F19.opExtrude","CAP_EDGE",EDGE,{"disambiguationData":[OSD([sQuery(id+"F18.wireOp",EDGE,"E25.left")])],"isStart":true});
            var Q7;
            Q7=makeQuery(id+"F12.opExtrude","SWEPT_EDGE",EDGE,{"disambiguationData":[OSD([sQuery(id+"F3.wireOp",EDGE,"E7.bottom"),sQuery(id+"F3.wireOp",EDGE,"E15.bottom"),sQuery(id+"F3.wireOp",EDGE,"E15.left")])]});
            var Q8;
            Q8=makeQuery(id+"F12.opExtrude","SWEPT_EDGE",EDGE,{"disambiguationData":[OSD([sQuery(id+"F3.wireOp",EDGE,"E7.bottom"),sQuery(id+"F3.wireOp",EDGE,"E15.bottom"),sQuery(id+"F3.wireOp",EDGE,"E15.right")])]});
            var Q9;
            Q9=makeQuery(id+"F12.opExtrude","SWEPT_EDGE",EDGE,{"disambiguationData":[OSD([sQuery(id+"F3.wireOp",EDGE,"E7.right"),sQuery(id+"F3.wireOp",EDGE,"E14.bottom"),sQuery(id+"F3.wireOp",EDGE,"E14.left")])]});
            var Q10;
            Q10=makeQuery(id+"F12.opExtrude","SWEPT_EDGE",EDGE,{"disambiguationData":[OSD([sQuery(id+"F3.wireOp",EDGE,"E7.right"),sQuery(id+"F3.wireOp",EDGE,"E14.top"),sQuery(id+"F3.wireOp",EDGE,"E14.left")])]});
            var Q11;
            Q11=makeQuery(id+"F12.opExtrude","SWEPT_EDGE",EDGE,{"disambiguationData":[OSD([sQuery(id+"F3.wireOp",EDGE,"E7.right"),sQuery(id+"F3.wireOp",EDGE,"E21.bottom"),sQuery(id+"F3.wireOp",EDGE,"E21.left")])]});
            var Q12;
            Q12=makeQuery(id+"F12.opExtrude","SWEPT_EDGE",EDGE,{"disambiguationData":[OSD([sQuery(id+"F3.wireOp",EDGE,"E7.top"),sQuery(id+"F3.wireOp",EDGE,"E21.left")])]});
            var Q13;
            Q13=makeQuery(id+"F12.opExtrude","SWEPT_EDGE",EDGE,{"disambiguationData":[OSD([sQuery(id+"F3.wireOp",EDGE,"E7.top"),sQuery(id+"F3.wireOp",EDGE,"E19.bottom"),sQuery(id+"F3.wireOp",EDGE,"E19.right")])]});
            fillet(context, id + "F22", {"entities" : qUnion([Q0, Q1, Q2, Q3, Q4, Q5, Q6, Q7, Q8, Q9, Q10, Q11, Q12, Q13]), "radius" : 5 * mm, "tangentPropagation" : true, "allowEdgeOverflow" : false});
        }
        {
            var Q0;
            Q0=makeQuery(id+"F21.opExtrude","CAP_EDGE",EDGE,{"disambiguationData":[OSD([sQuery(id+"F20.wireOp",EDGE,"E30")])],"isStart":true});
            var Q1;
            Q1=makeQuery(id+"F21.opExtrude","CAP_EDGE",EDGE,{"disambiguationData":[OSD([sQuery(id+"F20.wireOp",EDGE,"E29")])],"isStart":true});
            var Q2;
            Q2=makeQuery(id+"F21.opExtrude","CAP_EDGE",EDGE,{"disambiguationData":[OSD([sQuery(id+"F20.wireOp",EDGE,"E28")])],"isStart":true});
            var Q3;
            Q3=makeQuery(id+"F21.opExtrude","CAP_EDGE",EDGE,{"disambiguationData":[OSD([sQuery(id+"F20.wireOp",EDGE,"E31")])],"isStart":true});
            var Q4;
            Q4=makeQuery(id+"F21.opExtrude","CAP_EDGE",EDGE,{"disambiguationData":[OSD([sQuery(id+"F20.wireOp",EDGE,"E32")])],"isStart":true});
            var Q5;
            Q5=makeQuery(id+"F21.opExtrude","CAP_EDGE",EDGE,{"disambiguationData":[OSD([sQuery(id+"F20.wireOp",EDGE,"E27")])],"isStart":true});
            chamfer(context, id + "F23", {"entities" : qUnion([Q0, Q1, Q2, Q3, Q4, Q5]), "width" : 1 * mm, "tangentPropagation" : true});
        }
    });
